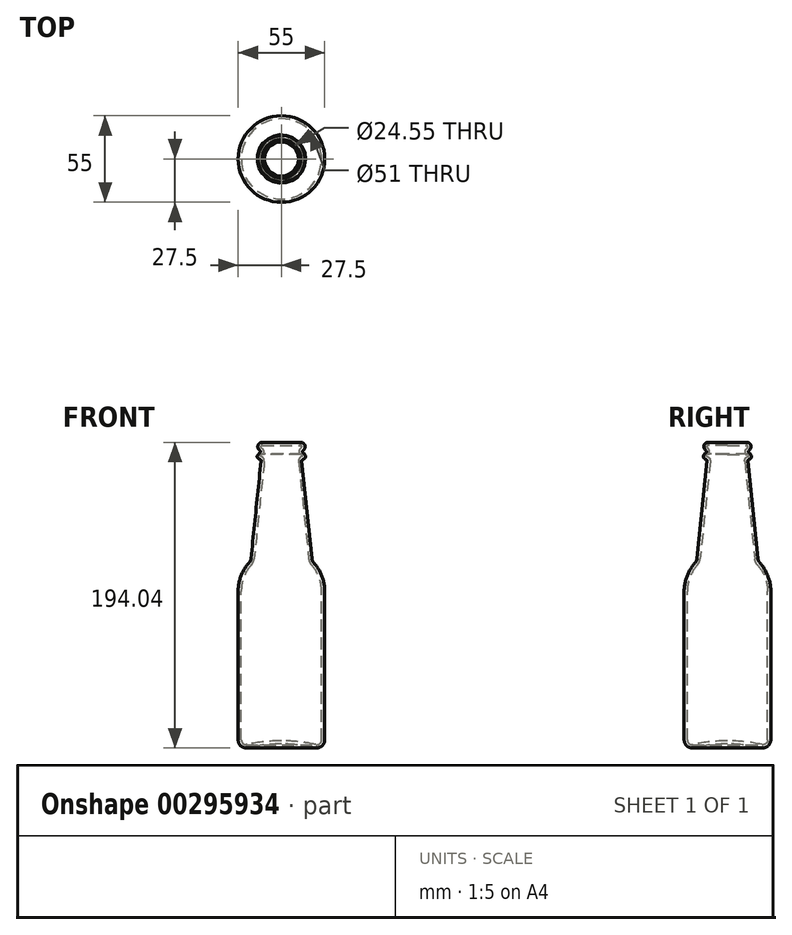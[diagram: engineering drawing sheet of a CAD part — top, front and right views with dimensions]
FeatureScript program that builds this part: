
annotation { "Feature Type Name" : "Feature", "Feature Type Description" : "" }
export const myFeature = defineFeature(function(context is Context, id is Id, definition is map)
    precondition{}
    {
        {
            var Q0;
            Q0=qCreatedBy(makeId("Front.planeOp"),FACE);
            var sketch = newSketch(context, id + "F0", { "sketchPlane" : qUnion([Q0])});
            skLineSegment(sketch, "E0.bottom", {"start": v(27.5, 0) * mm, "end": v(-27.5, 0) * mm, "construction": true});
            skLineSegment(sketch, "E0.top", {"start": v(27.5, 120) * mm, "end": v(-27.5, 120) * mm, "construction": true});
            skLineSegment(sketch, "E0.left", {"start": v(27.5, 6.42) * mm, "end": v(27.5, 120) * mm, "construction": true});
            skLineSegment(sketch, "E0.right", {"start": v(-27.5, 6.42) * mm, "end": v(-27.5, 120) * mm, "construction": true});
            skPoint(sketch, "E0.middle", {"position": v(0, 60) * mm});
            skLineSegment(sketch, "E1", {"start": v(-19.5, 120) * mm, "end": v(-12, 195.5) * mm, "construction": true});
            skLineSegment(sketch, "E2", {"start": v(-12, 195.5) * mm, "end": v(12, 195.5) * mm, "construction": true});
            skLineSegment(sketch, "E3", {"start": v(12, 195.5) * mm, "end": v(19.5, 120) * mm, "construction": true});
            skLineSegment(sketch, "E4", {"start": v(0, 120) * mm, "end": v(0, 195.5) * mm, "construction": true});
            skLineSegment(sketch, "E5", {"start": v(-12.27, 192.75) * mm, "end": v(12.27, 192.75) * mm, "construction": true});
            skLineSegment(sketch, "E6", {"start": v(-12.82, 187.25) * mm, "end": v(12.82, 187.25) * mm, "construction": true});
            skArc(sketch, "E7.0.startCap", {"start": v(-12.27, 190) * mm, "mid": v(-15.02, 192.75) * mm, "end": v(-12.27, 195.5) * mm, "construction": true});
            skArc(sketch, "E7.0.endCap", {"start": v(12.27, 195.5) * mm, "mid": v(15.02, 192.75) * mm, "end": v(12.27, 190) * mm});
            skLineSegment(sketch, "E7.0.left", {"start": v(-12.27, 195.5) * mm, "end": v(12.27, 195.5) * mm});
            skLineSegment(sketch, "E7.0.right", {"start": v(-12.27, 190) * mm, "end": v(12.27, 190) * mm, "construction": true});
            skArc(sketch, "E8.0.startCap", {"start": v(-12.82, 184.5) * mm, "mid": v(-15.57, 187.25) * mm, "end": v(-12.82, 190) * mm, "construction": true});
            skArc(sketch, "E8.0.endCap", {"start": v(15.27, 186) * mm, "mid": v(14.25, 184.9) * mm, "end": v(12.82, 184.5) * mm});
            skLineSegment(sketch, "E8.0.left", {"start": v(-12.82, 190) * mm, "end": v(12.82, 190) * mm, "construction": true});
            skLineSegment(sketch, "E8.0.right", {"start": v(-12.82, 184.5) * mm, "end": v(12.82, 184.5) * mm, "construction": true});
            skLineSegment(sketch, "E9", {"start": v(12.82, 190) * mm, "end": v(12.27, 190) * mm});
            skLineSegment(sketch, "E10", {"start": v(-12.82, 190) * mm, "end": v(-12.27, 190) * mm, "construction": true});
            skLineSegment(sketch, "E11", {"start": v(-12.82, 184.5) * mm, "end": v(-19.5, 120) * mm, "construction": true});
            skLineSegment(sketch, "E12", {"start": v(-19.5, 120) * mm, "end": v(-27.5, 120) * mm, "construction": true});
            skLineSegment(sketch, "E13", {"start": v(-27.5, 120) * mm, "end": v(-27.5, 0) * mm, "construction": true});
            skArc(sketch, "E14", {"start": v(21.43, 1.53) * mm, "mid": v(0, 3.86) * mm, "end": v(-21.43, 1.53) * mm});
            skLineSegment(sketch, "E15", {"start": v(27.5, 0) * mm, "end": v(27.5, 120) * mm});
            skLineSegment(sketch, "E16", {"start": v(27.5, 120) * mm, "end": v(19.5, 120) * mm});
            skLineSegment(sketch, "E17", {"start": v(19.5, 120) * mm, "end": v(12.82, 184.5) * mm});
            skPoint(sketch, "E18.visualSharp", {"position": v(27.5, 0) * mm});
            skArc(sketch, "E18.filletArc", {"start": v(21.43, 1.53) * mm, "mid": v(25.63, 2.52) * mm, "end": v(27.5, 6.42) * mm});
            skPoint(sketch, "E19.visualSharp", {"position": v(-27.5, 0) * mm});
            skArc(sketch, "E19.filletArc", {"start": v(-27.5, 6.42) * mm, "mid": v(-25.63, 2.52) * mm, "end": v(-21.43, 1.53) * mm, "construction": true});
            skLineSegment(sketch, "E20", {"start": v(0, 195.5) * mm, "end": v(0, 3.86) * mm});
            skLineSegment(sketch, "E21", {"start": v(12.82, 190) * mm, "end": v(15.16, 187.08) * mm});
            skPoint(sketch, "E22.visualSharp", {"position": v(15.5, 186.64) * mm});
            skArc(sketch, "E22.filletArc", {"start": v(15.27, 186) * mm, "mid": v(15.37, 186.55) * mm, "end": v(15.16, 187.08) * mm});
            skSolve(sketch);
        }
        {
            var Q0;
            Q0 = qSketchRegion(id + "F0", true);
            var Q1;
            Q1=sQuery(id+"F0.wireOp",EDGE,"E20");
            revolve(context, id + "F1", {"entities" : qUnion([Q0]), "axis" : qUnion([Q1]), "revolveType" : RevolveType.FULL});
        }
        {
            var Q0;
            Q0=makeQuery(id+"F1.opRevolve","SWEPT_EDGE",EDGE,{"disambiguationData":[OSD([sQuery(id+"F0.wireOp",EDGE,"E15"),sQuery(id+"F0.wireOp",EDGE,"E16")])]});
            fillet(context, id + "F2", {"entities" : qUnion([Q0]), "radius" : 27 * mm, "tangentPropagation" : true, "allowEdgeOverflow" : false});
        }
        {
            var Q0;
            Q0=makeQuery(id+"F2.opFillet","BLEND_EDGE",EDGE,{"blendedFrom":[makeQuery(id+"F1.opRevolve","SWEPT_EDGE",EDGE,{"disambiguationData":[OSD([sQuery(id+"F0.wireOp",EDGE,"E15"),sQuery(id+"F0.wireOp",EDGE,"E16")])]}),makeQuery(id+"F1.opRevolve","SWEPT_FACE",FACE,{"disambiguationData":[OSD([sQuery(id+"F0.wireOp",EDGE,"E17")])]})],"blendedInto":[makeQuery(id+"F1.opRevolve","SWEPT_FACE",FACE,{"disambiguationData":[OSD([sQuery(id+"F0.wireOp",EDGE,"E17")])]})]});
            fillet(context, id + "F3", {"entities" : qUnion([Q0]), "radius" : 5 * mm, "tangentPropagation" : true, "allowEdgeOverflow" : false});
        }
        {
            var Q0;
            Q0=makeQuery(id+"F1.opRevolve","SWEPT_EDGE",EDGE,{"disambiguationData":[OSD([sQuery(id+"F0.wireOp",EDGE,"E8.0.endCap"),sQuery(id+"F0.wireOp",EDGE,"E17")])]});
            fillet(context, id + "F4", {"entities" : qUnion([Q0]), "radius" : 1 * mm, "tangentPropagation" : true, "allowEdgeOverflow" : false});
        }
        {
            var Q0;
            Q0=makeQuery(id+"F1.opRevolve","SWEPT_FACE",FACE,{"disambiguationData":[OSD([sQuery(id+"F0.wireOp",EDGE,"E7.0.endCap")])]});
            fillet(context, id + "F5", {"entities" : qUnion([Q0]), "radius" : 30 * mm, "tangentPropagation" : true, "allowEdgeOverflow" : false});
        }
        {
            var Q0;
            Q0=makeQuery(id+"F5.opFillet","BLEND_EDGE",EDGE,{"blendedFrom":[makeQuery(id+"F1.opRevolve","SWEPT_EDGE",EDGE,{"disambiguationData":[OSD([sQuery(id+"F0.wireOp",EDGE,"E7.0.endCap"),sQuery(id+"F0.wireOp",EDGE,"E9")])]}),makeQuery(id+"F1.opRevolve","SWEPT_FACE",FACE,{"disambiguationData":[OSD([sQuery(id+"F0.wireOp",EDGE,"E21")])]})],"blendedInto":[makeQuery(id+"F1.opRevolve","SWEPT_FACE",FACE,{"disambiguationData":[OSD([sQuery(id+"F0.wireOp",EDGE,"E21")])]})]});
            fillet(context, id + "F6", {"entities" : qUnion([Q0]), "radius" : 2 * mm, "tangentPropagation" : true, "rho" : .8, "crossSection" : FilletCrossSection.CONIC, "allowEdgeOverflow" : false});
        }
        {
            var Q0;
            Q0=makeQuery(id+"F1.opRevolve","SWEPT_FACE",FACE,{"disambiguationData":[OSD([sQuery(id+"F0.wireOp",EDGE,"E7.0.left")])]});
            shell(context, id + "F7", {"entities" : qUnion([Q0]), "thickness" : 2 * mm});
        }
        {
            var Q0;
            Q0=makeQuery(id+"F7.opShell","OFFSET_EDGE",EDGE,{"disambiguationData":[OSD([sQuery(id+"F0.wireOp",EDGE,"E7.0.endCap"),sQuery(id+"F0.wireOp",EDGE,"E7.0.left")]),OD(0.0)]});
            fillet(context, id + "F8", {"entities" : qUnion([Q0]), "radius" : 0.5 * mm, "tangentPropagation" : true, "rho" : 0.5, "crossSection" : FilletCrossSection.CONIC, "allowEdgeOverflow" : false});
        }
        {
            var Q0;
            Q0=sQuery(id+"F0.wireOp",EDGE,"E0.bottom");
            cPlane(context, id + "F9", {"entities" : qUnion([Q0]), "cplaneType" : CPlaneType.LINE_ANGLE, "offset" : 25 * mm, "angle" : 45 * degree, "width" : 150 * mm, "height" : 150 * mm});
        }
    });
